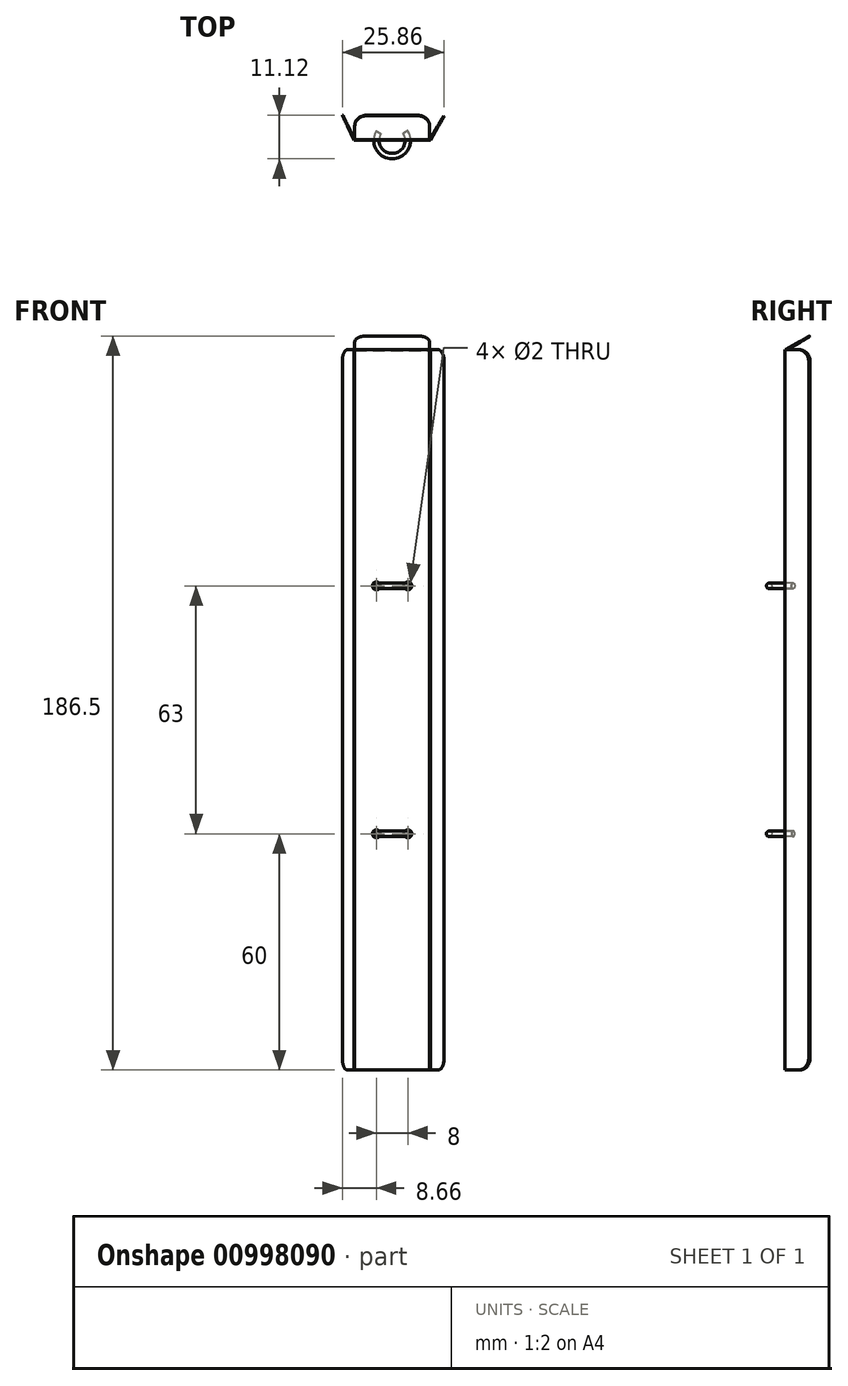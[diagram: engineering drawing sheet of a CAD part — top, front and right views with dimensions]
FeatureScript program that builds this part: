
annotation { "Feature Type Name" : "Feature", "Feature Type Description" : "" }
export const myFeature = defineFeature(function(context is Context, id is Id, definition is map)
    precondition{}
    {
        {
            var Q0;
            Q0=qCreatedBy(makeId("Front.planeOp"),FACE);
            var sketch = newSketch(context, id + "F0", { "sketchPlane" : qUnion([Q0])});
            skLineSegment(sketch, "E0.bottom", {"start": v(-9.5, 91.5) * mm, "end": v(9.5, 91.5) * mm});
            skLineSegment(sketch, "E0.top", {"start": v(-9.5, -91.5) * mm, "end": v(9.5, -91.5) * mm});
            skLineSegment(sketch, "E0.left", {"start": v(-9.5, 91.5) * mm, "end": v(-9.5, -91.5) * mm});
            skLineSegment(sketch, "E0.right", {"start": v(9.5, 91.5) * mm, "end": v(9.5, -91.5) * mm});
            skPoint(sketch, "E0.middle", {"position": v(0, 0) * mm});
            skSolve(sketch);
        }
        {
            var Q0;
            Q0 = qSketchRegion(id + "F0", true);
            extrude(context, id + "F1", {"entities" : qUnion([Q0]), "depth" : 0.2 * mm, "offsetDistance" : 25 * mm});
        }
        {
            var Q0;
            Q0=makeQuery(id+"F1.opExtrude","SWEPT_FACE",FACE,{"disambiguationData":[OSD([sQuery(id+"F0.wireOp",EDGE,"E0.right")])]});
            var sketch = newSketch(context, id + "F2", { "sketchPlane" : qUnion([Q0])});
            skLineSegment(sketch, "E1.bottom", {"start": v(-0.2, 91.5) * mm, "end": v(3.8, 91.5) * mm});
            skLineSegment(sketch, "E1.top", {"start": v(-0.2, -91.5) * mm, "end": v(3.8, -91.5) * mm});
            skLineSegment(sketch, "E1.left", {"start": v(-0.2, 91.5) * mm, "end": v(-0.2, -91.5) * mm});
            skLineSegment(sketch, "E1.right", {"start": v(6.8, 88.5) * mm, "end": v(6.8, -88.5) * mm});
            skPoint(sketch, "E2.visualSharp", {"position": v(6.8, 91.5) * mm});
            skArc(sketch, "E2.filletArc", {"start": v(6.8, 88.5) * mm, "mid": v(5.92, 90.62) * mm, "end": v(3.8, 91.5) * mm});
            skPoint(sketch, "E3.visualSharp", {"position": v(6.8, -91.5) * mm});
            skArc(sketch, "E3.filletArc", {"start": v(3.8, -91.5) * mm, "mid": v(5.92, -90.62) * mm, "end": v(6.8, -88.5) * mm});
            skSolve(sketch);
        }
        {
            var Q0;
            Q0 = qSketchRegion(id + "F2", true);
            extrude(context, id + "F3", {"entities" : qUnion([Q0]), "depth" : 0.2 * mm, "offsetDistance" : 25 * mm});
        }
        {
            var Q0;
            Q0=makeQuery(id+"F3.opExtrude","SWEPT_BODY",BODY,{"disambiguationData":[OSD([sQuery(id+"F2.wireOp",EDGE,"E1.bottom"),sQuery(id+"F2.wireOp",EDGE,"E1.top"),sQuery(id+"F2.wireOp",EDGE,"E1.left"),sQuery(id+"F2.wireOp",EDGE,"E1.right"),sQuery(id+"F2.wireOp",EDGE,"E2.filletArc"),sQuery(id+"F2.wireOp",EDGE,"E3.filletArc")])]});
            transform(context, id + "F4", {"entities" : qUnion([Q0]), "transformType" : TransformType.TRANSLATION_3D, "dx" : -19.2 * mm, "dy" : 0 * mm, "dz" : 0 * mm, "makeCopy" : true});
        }
        {
            var Q0;
            Q0=makeQuery(id+"F3.boolean.opBoolean","MERGE",FACE,{"derivedFrom":[makeQuery(id+"F1.opExtrude","CAP_FACE",FACE,{"disambiguationData":[OSD([sQuery(id+"F0.wireOp",EDGE,"E0.bottom"),sQuery(id+"F0.wireOp",EDGE,"E0.top"),sQuery(id+"F0.wireOp",EDGE,"E0.left"),sQuery(id+"F0.wireOp",EDGE,"E0.right")])],"isStart":false}),makeQuery(id+"F3.opExtrude","SWEPT_FACE",FACE,{"disambiguationData":[OSD([sQuery(id+"F2.wireOp",EDGE,"E1.left")])]})]});
            var sketch = newSketch(context, id + "F5", { "sketchPlane" : qUnion([Q0])});
            skCircle(sketch, "E4", {"center": v(-4, 31.5) * mm, "radius": 1 * mm});
            skCircle(sketch, "E5.MirrorC", {"center": v(4, 31.5) * mm, "radius": 1 * mm});
            skCircle(sketch, "E6.MirrorC", {"center": v(-4, -31.5) * mm, "radius": 1 * mm});
            skCircle(sketch, "E7.MirrorC", {"center": v(4, -31.5) * mm, "radius": 1 * mm});
            skSolve(sketch);
        }
        {
            var Q0;
            Q0=sQuery(id+"F5.wireOp",VERTEX,"E4.center");
            var Q1;
            Q1=sQuery(id+"F5.wireOp",VERTEX,"E5.MirrorC.center");
            var Q2;
            Q2=sQuery(id+"F5.wireOp",VERTEX,"E7.MirrorC.center");
            var Q3;
            Q3=sQuery(id+"F5.wireOp",VERTEX,"E6.MirrorC.center");
            var Q4;
            Q4=makeQuery(id+"F1.opExtrude","SWEPT_BODY",BODY,{"disambiguationData":[OSD([sQuery(id+"F0.wireOp",EDGE,"E0.bottom"),sQuery(id+"F0.wireOp",EDGE,"E0.top"),sQuery(id+"F0.wireOp",EDGE,"E0.left"),sQuery(id+"F0.wireOp",EDGE,"E0.right")])]});
            hole(context, id + "F6", {"style" : HoleStyle.SIMPLE, "endStyle" : HoleEndStyle.THROUGH, "holeDiameter" : 2 * mm, "majorDiameter" : 5 * mm, "isTappedThrough" : true, "tappedDepth" : 12 * mm, "tapClearance" : 3, "locations" : qUnion([Q0, Q1, Q2, Q3]), "scope" : qUnion([Q4])});
        }
        {
            var Q0;
            Q0=makeQuery(id+"F3.boolean.opBoolean","MERGE",FACE,{"derivedFrom":[makeQuery(id+"F1.opExtrude","CAP_FACE",FACE,{"disambiguationData":[OSD([sQuery(id+"F0.wireOp",EDGE,"E0.bottom"),sQuery(id+"F0.wireOp",EDGE,"E0.top"),sQuery(id+"F0.wireOp",EDGE,"E0.left"),sQuery(id+"F0.wireOp",EDGE,"E0.right")])],"isStart":false}),makeQuery(id+"F3.opExtrude","SWEPT_FACE",FACE,{"disambiguationData":[OSD([sQuery(id+"F2.wireOp",EDGE,"E1.left")])]})]});
            var sketch = newSketch(context, id + "F7", { "sketchPlane" : qUnion([Q0])});
            skCircle(sketch, "E8", {"center": v(-4, 31.5) * mm, "radius": 0.69 * mm});
            skLineSegment(sketch, "E9", {"start": v(0, 74.96) * mm, "end": v(0, 0) * mm, "construction": true});
            skSolve(sketch);
        }
        {
            var Q0;
            Q0=makeQuery(id+"F7.imprint","IMPRINT",FACE,{"disambiguationData":[TD([[makeQuery(id+"F7.imprint","IMPRINT",EDGE,{"derivedFrom":sQuery(id+"F7.wireOp",EDGE,"E8")}),1.0]])]});
            var Q1;
            Q1=sQuery(id+"F7.wireOp",EDGE,"E9");
            revolve(context, id + "F8", {"surfaceOperationType" : NewSurfaceOperationType.NEW, "entities" : qUnion([Q0]), "axis" : qUnion([Q1]), "revolveType" : RevolveType.TWO_DIRECTIONS, "angle" : 30 * degree, "angleBack" : 147.55 * degree});
        }
        {
            var Q0;
            Q0=makeQuery(id+"F8.opRevolve","SWEPT_BODY",BODY,{"disambiguationData":[OSD([sQuery(id+"F7.wireOp",EDGE,"E8")])]});
            var Q1;
            Q1=qCreatedBy(makeId("Top.planeOp"),FACE);
            mirror(context, id + "F9", {"entities" : qUnion([Q0]), "mirrorPlane" : qUnion([Q1])});
        }
        {
            var Q0;
            Q0=makeQuery(id+"F3.opExtrude","SWEPT_BODY",BODY,{"disambiguationData":[OSD([sQuery(id+"F2.wireOp",EDGE,"E1.bottom"),sQuery(id+"F2.wireOp",EDGE,"E1.top"),sQuery(id+"F2.wireOp",EDGE,"E1.left"),sQuery(id+"F2.wireOp",EDGE,"E1.right"),sQuery(id+"F2.wireOp",EDGE,"E2.filletArc"),sQuery(id+"F2.wireOp",EDGE,"E3.filletArc")])]});
            var Q1;
            Q1=makeQuery(id+"F3.opExtrude","CAP_EDGE",EDGE,{"disambiguationData":[OSD([sQuery(id+"F2.wireOp",EDGE,"E1.left")])],"isStart":false});
            transform(context, id + "F10", {"entities" : qUnion([Q0]), "transformType" : TransformType.ROTATION, "transformAxis" : qUnion([Q1]), "angle" : 30 * degree, "makeCopy" : false});
        }
        {
            var Q0;
            Q0=makeQuery(id+"F1.opExtrude","SWEPT_FACE",FACE,{"disambiguationData":[OSD([sQuery(id+"F0.wireOp",EDGE,"E0.bottom")])]});
            var sketch = newSketch(context, id + "F11", { "sketchPlane" : qUnion([Q0])});
            skLineSegment(sketch, "E10.bottom", {"start": v(9.5, 0) * mm, "end": v(-9.5, 0) * mm});
            skLineSegment(sketch, "E10.top", {"start": v(6.5, 7) * mm, "end": v(-6.5, 7) * mm});
            skLineSegment(sketch, "E10.left", {"start": v(9.5, 0) * mm, "end": v(9.5, 4) * mm});
            skLineSegment(sketch, "E10.right", {"start": v(-9.5, 0) * mm, "end": v(-9.5, 4) * mm});
            skPoint(sketch, "E11.visualSharp", {"position": v(9.5, 7) * mm});
            skArc(sketch, "E11.filletArc", {"start": v(9.5, 4) * mm, "mid": v(8.62, 6.12) * mm, "end": v(6.5, 7) * mm});
            skPoint(sketch, "E12.visualSharp", {"position": v(-9.5, 7) * mm});
            skArc(sketch, "E12.filletArc", {"start": v(-6.5, 7) * mm, "mid": v(-8.62, 6.12) * mm, "end": v(-9.5, 4) * mm});
            skSolve(sketch);
        }
        {
            var Q0;
            Q0 = qSketchRegion(id + "F11", true);
            extrude(context, id + "F12", {"entities" : qUnion([Q0]), "oppositeDirection" : true, "depth" : 0.2 * mm, "offsetDistance" : 25 * mm});
        }
        {
            var Q0;
            Q0=makeQuery(id+"F12.opExtrude","SWEPT_BODY",BODY,{"disambiguationData":[OSD([sQuery(id+"F11.wireOp",EDGE,"E10.bottom"),sQuery(id+"F11.wireOp",EDGE,"E10.top"),sQuery(id+"F11.wireOp",EDGE,"E10.left"),sQuery(id+"F11.wireOp",EDGE,"E10.right"),sQuery(id+"F11.wireOp",EDGE,"E11.filletArc"),sQuery(id+"F11.wireOp",EDGE,"E12.filletArc")])]});
            var Q1;
            Q1=makeQuery(id+"F1.opExtrude","CAP_EDGE",EDGE,{"disambiguationData":[OSD([sQuery(id+"F0.wireOp",EDGE,"E0.bottom")])],"isStart":true});
            transform(context, id + "F13", {"entities" : qUnion([Q0]), "transformType" : TransformType.ROTATION, "transformAxis" : qUnion([Q1]), "angle" : 30 * degree, "makeCopy" : false});
        }
        {
            var Q0;
            Q0=makeQuery(id+"F4.opPattern","COPY",BODY,{"derivedFrom":makeQuery(id+"F3.opExtrude","SWEPT_BODY",BODY,{"disambiguationData":[OSD([sQuery(id+"F2.wireOp",EDGE,"E1.bottom"),sQuery(id+"F2.wireOp",EDGE,"E1.top"),sQuery(id+"F2.wireOp",EDGE,"E1.left"),sQuery(id+"F2.wireOp",EDGE,"E1.right"),sQuery(id+"F2.wireOp",EDGE,"E2.filletArc"),sQuery(id+"F2.wireOp",EDGE,"E3.filletArc")])]}),"instanceName":"1"});
            var Q1;
            Q1=makeQuery(id+"F4.opPattern","COPY",EDGE,{"derivedFrom":makeQuery(id+"F3.opExtrude","CAP_EDGE",EDGE,{"disambiguationData":[OSD([sQuery(id+"F2.wireOp",EDGE,"E1.left")])],"isStart":true}),"instanceName":"1"});
            transform(context, id + "F14", {"entities" : qUnion([Q0]), "transformType" : TransformType.ROTATION, "transformAxis" : qUnion([Q1]), "angle" : 25 * degree, "oppositeDirection" : true, "makeCopy" : false});
        }
    });
